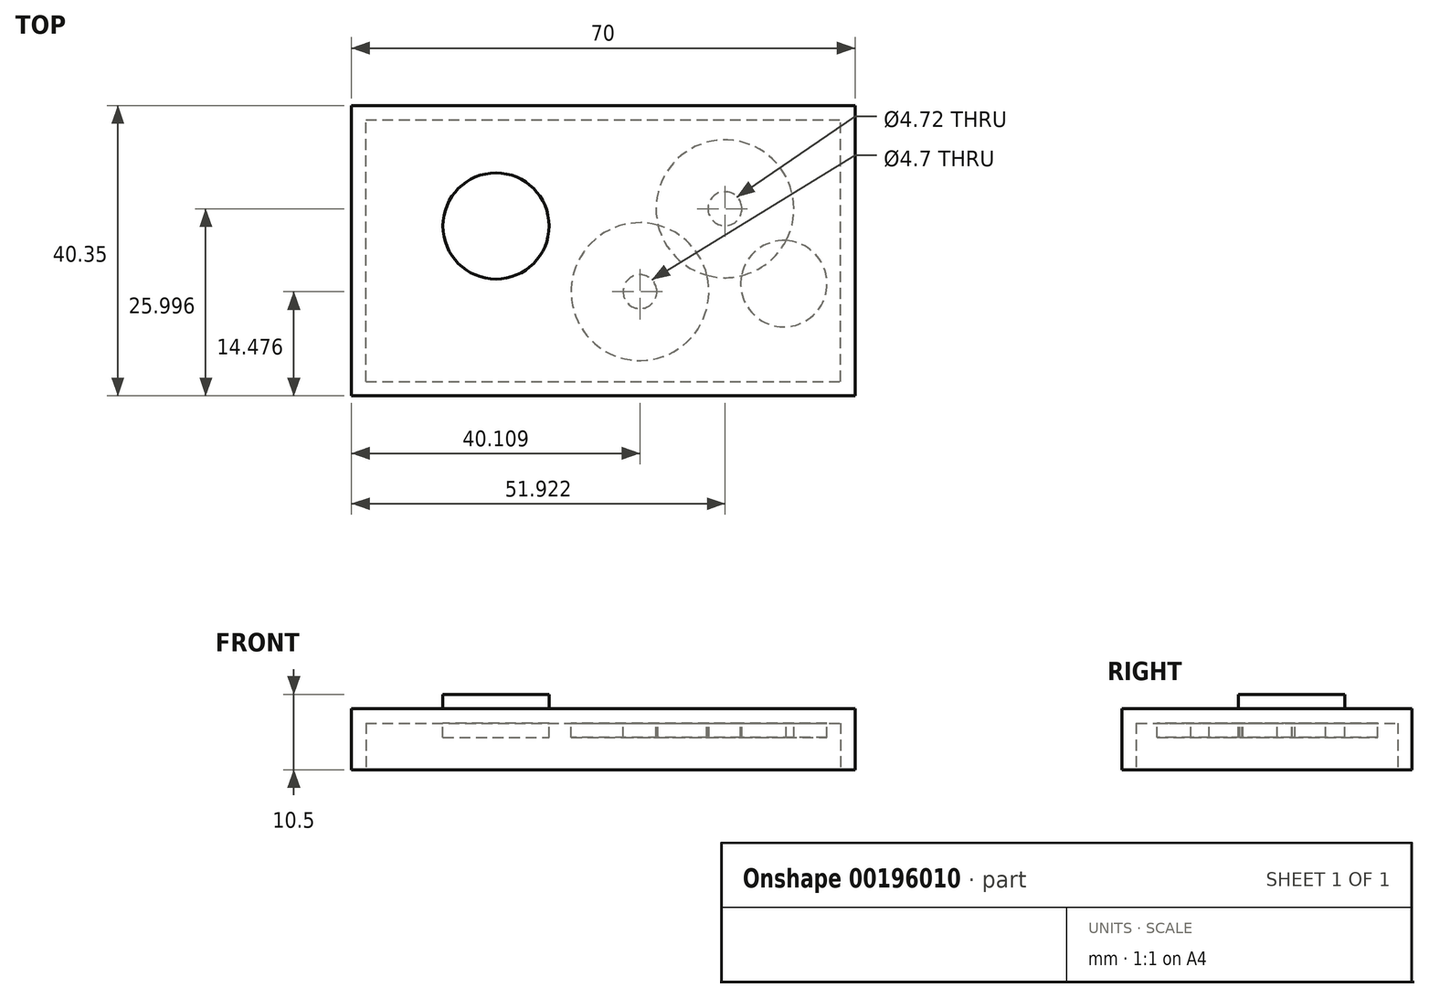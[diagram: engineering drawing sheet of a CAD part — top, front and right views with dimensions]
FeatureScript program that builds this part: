
annotation { "Feature Type Name" : "Feature", "Feature Type Description" : "" }
export const myFeature = defineFeature(function(context is Context, id is Id, definition is map)
    precondition{}
    {
        {
            var Q0;
            Q0=qCreatedBy(makeId("Top.planeOp"),FACE);
            var sketch = newSketch(context, id + "F0", { "sketchPlane" : qUnion([Q0])});
            skLineSegment(sketch, "E0.bottom", {"start": v(-35, 0) * mm, "end": v(35, 0) * mm});
            skLineSegment(sketch, "E0.top", {"start": v(-35, 40.35) * mm, "end": v(35, 40.35) * mm});
            skLineSegment(sketch, "E0.left", {"start": v(-35, 0) * mm, "end": v(-35, 40.35) * mm});
            skLineSegment(sketch, "E0.right", {"start": v(35, 0) * mm, "end": v(35, 40.35) * mm});
            skLineSegment(sketch, "E1.bottom", {"start": v(-29.27, 44.22) * mm, "end": v(40.73, 44.22) * mm});
            skLineSegment(sketch, "E1.top", {"start": v(-29.27, 83.66) * mm, "end": v(40.73, 83.66) * mm});
            skCircle(sketch, "E2", {"center": v(-6.9, 60.7) * mm, "radius": 7.38 * mm});
            skCircle(sketch, "E3", {"center": v(13.12, 69.82) * mm, "radius": 2.35 * mm});
            skCircle(sketch, "E4", {"center": v(24.94, 58.3) * mm, "radius": 2.36 * mm});
            skCircle(sketch, "E5", {"center": v(24.94, 58.3) * mm, "radius": 9.57 * mm});
            skCircle(sketch, "E6", {"center": v(13.12, 69.82) * mm, "radius": 9.57 * mm});
            skCircle(sketch, "E7", {"center": v(33.12, 68.72) * mm, "radius": 6 * mm});
            skSolve(sketch);
        }
        {
            var Q0;
            Q0=makeQuery(id+"F0.imprint","IMPRINT",FACE,{"disambiguationData":[TD([[makeQuery(id+"F0.imprint","IMPRINT",EDGE,{"derivedFrom":sQuery(id+"F0.wireOp",EDGE,"E0.bottom")}),1.0]])]});
            extrude(context, id + "F1", {"entities" : qUnion([Q0]), "depth" : 8.5 * mm});
        }
        {
            var Q0;
            Q0=makeQuery(id+"F1.opExtrude","CAP_FACE",FACE,{"disambiguationData":[OSD([sQuery(id+"F0.wireOp",EDGE,"E0.bottom"),sQuery(id+"F0.wireOp",EDGE,"E0.top"),sQuery(id+"F0.wireOp",EDGE,"E0.left"),sQuery(id+"F0.wireOp",EDGE,"E0.right")])],"isStart":true});
            shell(context, id + "F2", {"entities" : qUnion([Q0]), "thickness" : 2 * mm});
        }
        {
            var Q0;
            Q0=makeQuery(id+"F2.opShell","OFFSET_FACE",FACE,{"disambiguationData":[OSD([sQuery(id+"F0.wireOp",EDGE,"E0.bottom"),sQuery(id+"F0.wireOp",EDGE,"E0.top"),sQuery(id+"F0.wireOp",EDGE,"E0.left"),sQuery(id+"F0.wireOp",EDGE,"E0.right")])]});
            var sketch = newSketch(context, id + "F3", { "sketchPlane" : qUnion([Q0])});
            skLineSegment(sketch, "E8.bottom", {"start": v(-37.28, -40.08) * mm, "end": v(32.72, -40.08) * mm});
            skLineSegment(sketch, "E8.top", {"start": v(-37.28, -0.64) * mm, "end": v(32.72, -0.64) * mm});
            skCircle(sketch, "E9", {"center": v(-14.9, -23.6) * mm, "radius": 7.38 * mm});
            skCircle(sketch, "E10", {"center": v(5.1, -14.48) * mm, "radius": 2.35 * mm});
            skCircle(sketch, "E11", {"center": v(16.92, -26) * mm, "radius": 2.36 * mm});
            skCircle(sketch, "E12", {"center": v(16.92, -26) * mm, "radius": 9.57 * mm});
            skCircle(sketch, "E13", {"center": v(5.1, -14.48) * mm, "radius": 9.57 * mm});
            skCircle(sketch, "E14", {"center": v(25.1, -15.58) * mm, "radius": 6 * mm});
            skSolve(sketch);
        }
        {
            var Q0;
            Q0=makeQuery(id+"F3.imprint","IMPRINT",FACE,{"disambiguationData":[TD([[makeQuery(id+"F3.imprint","IMPRINT",EDGE,{"derivedFrom":sQuery(id+"F3.wireOp",EDGE,"E10")}),-1.0]])]});
            var Q1;
            Q1=makeQuery(id+"F3.imprint","IMPRINT",FACE,{"disambiguationData":[TD([[makeQuery(id+"F3.imprint","IMPRINT",EDGE,{"derivedFrom":sQuery(id+"F3.wireOp",EDGE,"E11")}),-1.0]])]});
            var Q2;
            {var subQ0=sQuery(id+"F3.wireOp",EDGE,"E14");var subQ1=sQuery(id+"F3.wireOp",EDGE,"E12");var subQ2=makeQuery(id+"F3.imprint","INTERSECT",VERTEX,{"disambiguationData":[OD(0.0)],"derivedFrom":[subQ1,subQ0]});Q2=makeQuery(id+"F3.imprint","IMPRINT",FACE,{"disambiguationData":[TD([[makeQuery(id+"F3.imprint","IMPRINT",EDGE,{"disambiguationData":[TD([[subQ2,1.0]])],"derivedFrom":subQ1}),-1.0]])]});}
            var Q3;
            Q3=makeQuery(id+"F3.imprint","IMPRINT",FACE,{"disambiguationData":[TD([[makeQuery(id+"F3.imprint","IMPRINT",EDGE,{"derivedFrom":sQuery(id+"F3.wireOp",EDGE,"E9")}),1.0]])]});
            extrude(context, id + "F4", {"entities" : qUnion([Q0, Q1, Q2, Q3]), "depth" : 2 * mm});
        }
        {
            var Q0;
            Q0=makeQuery(id+"F4.opExtrude","CAP_FACE",FACE,{"disambiguationData":[OSD([sQuery(id+"F3.wireOp",EDGE,"E9")])],"isStart":false});
            extrude(context, id + "F5", {"entities" : qUnion([Q0]), "operationType" : NewBodyOperationType.ADD, "oppositeDirection" : true, "depth" : 6 * mm});
        }
    });
